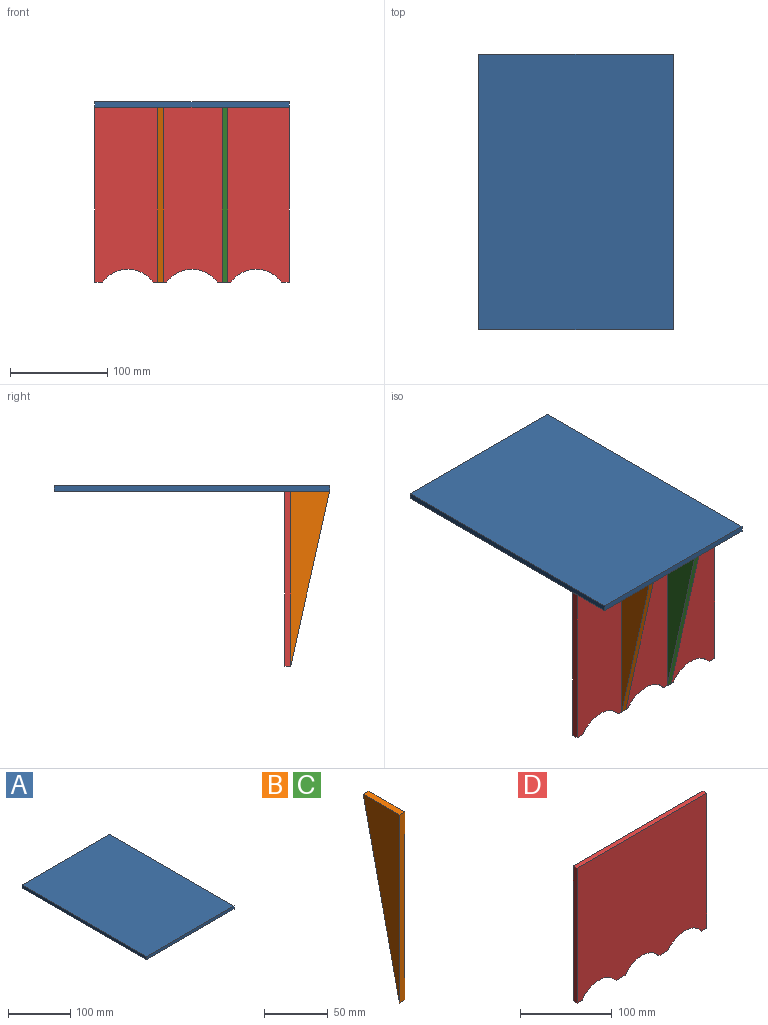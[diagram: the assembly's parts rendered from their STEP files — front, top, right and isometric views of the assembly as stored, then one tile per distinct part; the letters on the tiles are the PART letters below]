
ASSEMBLY  parts=4 mates=2
PART A: 6 faces, bbox 200x283x6 mm
  f0: plane 200x6mm, normal (0,1,0), area 1200mm2, adj f1,f3,f4,f5
  f1: plane 283x6mm, normal (-1,0,0), area 1698mm2, adj f0,f2,f4,f5
  f2: plane 200x6mm, normal (0,-1,0), area 1200mm2, adj f1,f3,f4,f5
  f3: plane 283x6mm, normal (1,0,0), area 1698mm2, adj f0,f2,f4,f5
  f4: plane 283x200mm, normal (0,0,1), area 56600mm2, adj f0,f1,f2,f3
  f5: plane 283x200mm, normal (0,0,-1), area 56600mm2, adj f0,f1,f2,f3
PART B: 5 faces, bbox 6x40x180 mm
  f0: plane 180x6mm, normal (0,-1,0), area 1080mm2, adj f1,f2,f3,f4
  f1: plane 180x40mm, normal (0,0.98,-0.22), area 1106.3mm2, adj f0,f2,f3,f4
  f2: plane 40x6mm, normal (0,0,1), area 240mm2, adj f0,f1,f3,f4
  f3: plane 180x40mm, normal (1,0,0), area 3600mm2, adj f0,f1,f2
  f4: plane 180x40mm, normal (-1,0,0), area 3600mm2, adj f0,f1,f2
PART C: same geometry as B
PART D: 12 faces, bbox 200x6x180 mm
  f0: plane 7.89x6mm, normal (0,0,-1), area 47.3mm2, adj f1,f9,f10,f11
  f1: cylinder r=32mm len=52.22mm, axis (0,1,0), area 366.5mm2, adj f0,f2,f10,f11
  f2: plane 13.78x6mm, normal (0,0,-1), area 82.7mm2, adj f1,f3,f10,f11
  f3: cylinder r=32mm len=52.22mm, axis (0,1,0), area 366.5mm2, adj f2,f4,f10,f11
  f4: plane 13.78x6mm, normal (0,0,-1), area 82.7mm2, adj f3,f5,f10,f11
  f5: cylinder r=32mm len=52.22mm, axis (0,1,0), area 366.5mm2, adj f4,f6,f10,f11
  f6: plane 7.89x6mm, normal (0,0,-1), area 47.3mm2, adj f5,f7,f10,f11
  f7: plane 180x6mm, normal (1,0,0), area 1080mm2, adj f6,f8,f10,f11
  f8: plane 200x6mm, normal (0,0,1), area 1200mm2, adj f7,f9,f10,f11
  f9: plane 180x6mm, normal (-1,0,0), area 1080mm2, adj f0,f8,f10,f11
  f10: plane 200x180mm, normal (0,-1,0), area 34517.3mm2, adj f0,f1,f2,f3,f4,f5,f6,f7
  f11: plane 200x180mm, normal (0,1,0), area 34517.3mm2, adj f0,f1,f2,f3,f4,f5,f6,f7
PLACE A rot(axis=(1,0,0),0deg) t=(-39.82,21.93,73.5)mm
PLACE B rot(axis=(0,0,1),180deg) t=(-68.82,11.65,-6.1)mm
PLACE C rot(axis=(0,0,1),180deg) t=(-2.82,11.65,-6.1)mm
PLACE D t=(-39.82,17.65,-16.5)mm
MATE fastened A.f5 <-> D.f8  axis (0,0,-1) through (60.18,-28.35,73.5)mm
MATE fastened C.f2 <-> A.f5  axis (0,0,1) through (-2.82,-28.35,73.5)mm
